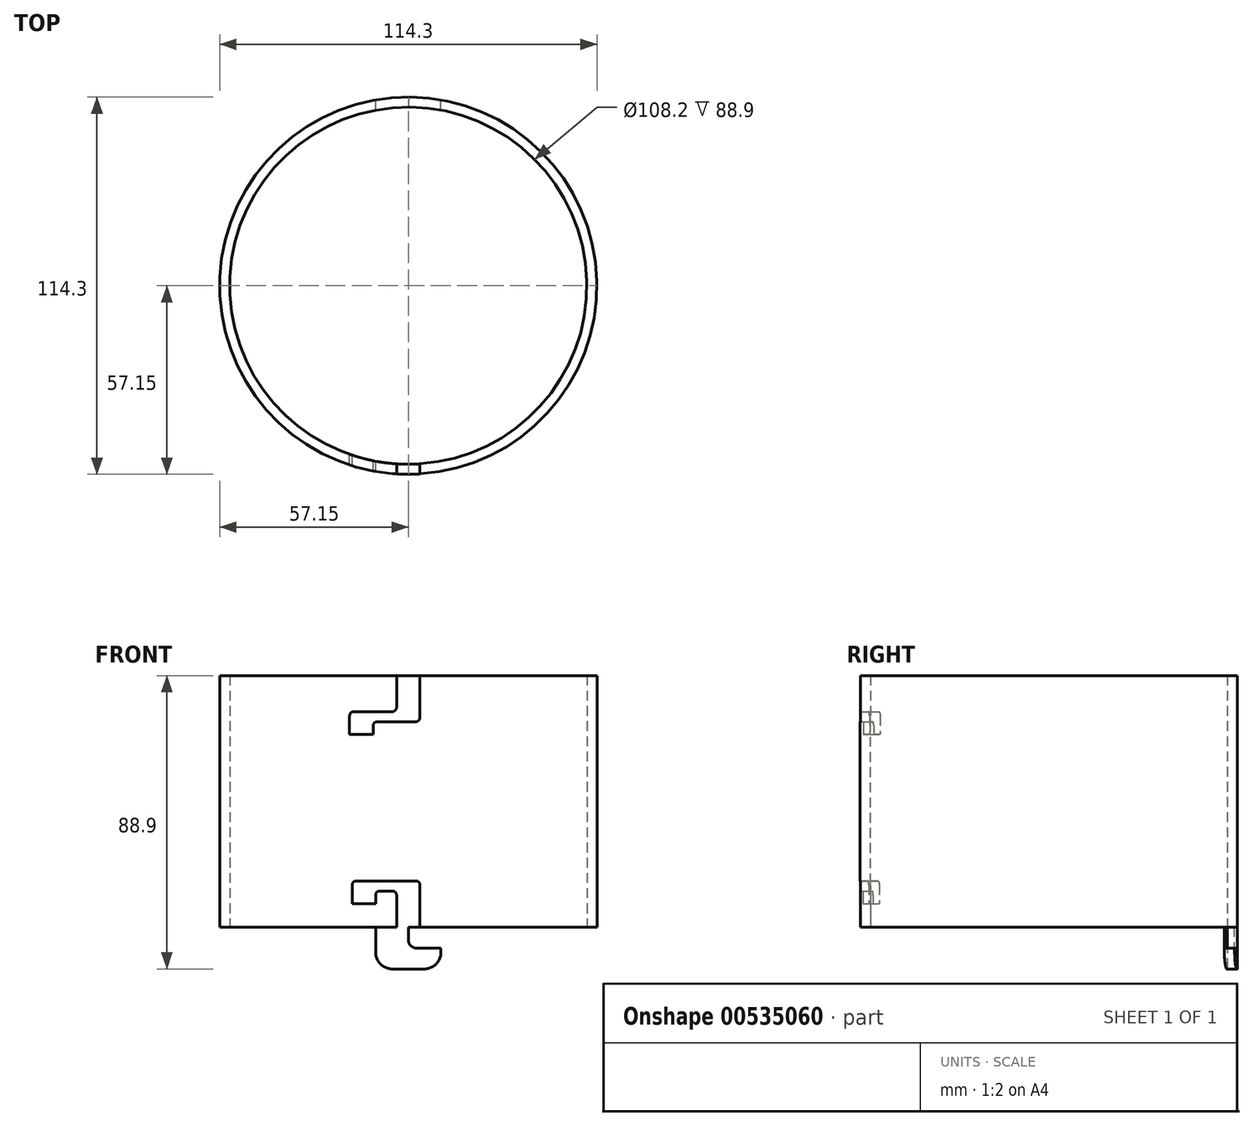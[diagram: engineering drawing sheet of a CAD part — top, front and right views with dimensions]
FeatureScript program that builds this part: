
annotation { "Feature Type Name" : "Feature", "Feature Type Description" : "" }
export const myFeature = defineFeature(function(context is Context, id is Id, definition is map)
    precondition{}
    {
        {
            var Q0;
            Q0=qCreatedBy(makeId("Top.planeOp"),FACE);
            var sketch = newSketch(context, id + "F0", { "sketchPlane" : qUnion([Q0])});
            skCircle(sketch, "E0", {"center": v(0, 0) * mm, "radius": 54.1 * mm});
            skCircle(sketch, "E1", {"center": v(0, 0) * mm, "radius": 57.15 * mm});
            skSolve(sketch);
        }
        {
            var Q0;
            Q0 = qSketchRegion(id + "F0", true);
            extrude(context, id + "F1", {"entities" : qUnion([Q0]), "depth" : 76.2 * mm, "offsetDistance" : 25.4 * mm, "symmetric" : true});
        }
        {
            var Q0;
            Q0=qCreatedBy(makeId("Front.planeOp"),FACE);
            var sketch = newSketch(context, id + "F2", { "sketchPlane" : qUnion([Q0])});
            skLineSegment(sketch, "E2", {"start": v(-3.56, -38.1) * mm, "end": v(-3.56, -27.18) * mm});
            skLineSegment(sketch, "E3", {"start": v(-3.56, -27.18) * mm, "end": v(-9.9, -27.18) * mm});
            skLineSegment(sketch, "E4", {"start": v(-9.9, -27.18) * mm, "end": v(-9.9, -30.99) * mm});
            skLineSegment(sketch, "E5", {"start": v(-9.9, -30.99) * mm, "end": v(-17.02, -30.99) * mm});
            skLineSegment(sketch, "E6", {"start": v(-17.02, -30.99) * mm, "end": v(-17.02, -24.13) * mm});
            skLineSegment(sketch, "E7", {"start": v(-17.02, -24.13) * mm, "end": v(3.56, -24.13) * mm});
            skLineSegment(sketch, "E8", {"start": v(3.56, -24.13) * mm, "end": v(3.56, -38.1) * mm});
            skPoint(sketch, "E9", {"position": v(0, -38.1) * mm});
            skPoint(sketch, "E10", {"position": v(3.56, -38.1) * mm});
            skPoint(sketch, "E11", {"position": v(-3.56, -38.1) * mm});
            skLineSegment(sketch, "E12", {"start": v(-3.56, -38.1) * mm, "end": v(3.56, -38.1) * mm});
            skPoint(sketch, "E13.MirrorP", {"position": v(-3.56, 38.1) * mm});
            skLineSegment(sketch, "E14.MirrorCS", {"start": v(-3.56, 38.1) * mm, "end": v(3.56, 38.1) * mm});
            skLineSegment(sketch, "E15.MirrorCS", {"start": v(3.56, 24.13) * mm, "end": v(3.56, 38.1) * mm});
            skLineSegment(sketch, "E16.MirrorCS", {"start": v(-3.56, 38.1) * mm, "end": v(-3.56, 27.18) * mm});
            skLineSegment(sketch, "E17", {"start": v(-3.56, 27.18) * mm, "end": v(-17.78, 27.18) * mm});
            skLineSegment(sketch, "E18", {"start": v(-17.78, 27.18) * mm, "end": v(-17.78, 20.32) * mm});
            skLineSegment(sketch, "E19", {"start": v(-17.78, 20.32) * mm, "end": v(-10.67, 20.32) * mm});
            skLineSegment(sketch, "E20", {"start": v(-10.67, 20.32) * mm, "end": v(-10.67, 24.13) * mm});
            skLineSegment(sketch, "E21", {"start": v(-10.67, 24.13) * mm, "end": v(3.56, 24.13) * mm});
            skSolve(sketch);
        }
        {
            var Q0;
            Q0 = qSketchRegion(id + "F2", true);
            extrude(context, id + "F3", {"entities" : qUnion([Q0]), "operationType" : NewBodyOperationType.REMOVE, "depth" : 103.12 * mm, "offsetDistance" : 25.4 * mm});
        }
        {
            var Q0;
            Q0=makeQuery(id+"F3.boolean.opBoolean","COPY",EDGE,{"derivedFrom":makeQuery(id+"F3.opExtrude","SWEPT_EDGE",EDGE,{"disambiguationData":[OSD([sQuery(id+"F2.wireOp",EDGE,"E3"),sQuery(id+"F2.wireOp",EDGE,"E4")])]})});
            var Q1;
            Q1=makeQuery(id+"F3.boolean.opBoolean","COPY",EDGE,{"derivedFrom":makeQuery(id+"F3.opExtrude","SWEPT_EDGE",EDGE,{"disambiguationData":[OSD([sQuery(id+"F2.wireOp",EDGE,"E2"),sQuery(id+"F2.wireOp",EDGE,"E3")])]})});
            var Q2;
            Q2=makeQuery(id+"F3.boolean.opBoolean","COPY",EDGE,{"derivedFrom":makeQuery(id+"F3.opExtrude","SWEPT_EDGE",EDGE,{"disambiguationData":[OSD([sQuery(id+"F2.wireOp",EDGE,"E7"),sQuery(id+"F2.wireOp",EDGE,"E8")])]})});
            var Q3;
            Q3=makeQuery(id+"F3.boolean.opBoolean","COPY",EDGE,{"derivedFrom":makeQuery(id+"F3.opExtrude","SWEPT_EDGE",EDGE,{"disambiguationData":[OSD([sQuery(id+"F2.wireOp",EDGE,"E6"),sQuery(id+"F2.wireOp",EDGE,"E7")])]})});
            fillet(context, id + "F4", {"entities" : qUnion([Q0, Q1, Q2, Q3]), "radius" : 1.27 * mm, "tangentPropagation" : true, "allowEdgeOverflow" : false});
        }
        {
            var Q0;
            Q0=makeQuery(id+"F3.boolean.opBoolean","COPY",EDGE,{"derivedFrom":makeQuery(id+"F3.opExtrude","SWEPT_EDGE",EDGE,{"disambiguationData":[OSD([sQuery(id+"F2.wireOp",EDGE,"E20"),sQuery(id+"F2.wireOp",EDGE,"E21")])]})});
            var Q1;
            Q1=makeQuery(id+"F3.boolean.opBoolean","COPY",EDGE,{"derivedFrom":makeQuery(id+"F3.opExtrude","SWEPT_EDGE",EDGE,{"disambiguationData":[OSD([sQuery(id+"F2.wireOp",EDGE,"E15.MirrorCS"),sQuery(id+"F2.wireOp",EDGE,"E21")])]})});
            var Q2;
            Q2=makeQuery(id+"F3.boolean.opBoolean","COPY",EDGE,{"derivedFrom":makeQuery(id+"F3.opExtrude","SWEPT_EDGE",EDGE,{"disambiguationData":[OSD([sQuery(id+"F2.wireOp",EDGE,"E16.MirrorCS"),sQuery(id+"F2.wireOp",EDGE,"E17")])]})});
            var Q3;
            Q3=makeQuery(id+"F3.boolean.opBoolean","COPY",EDGE,{"derivedFrom":makeQuery(id+"F3.opExtrude","SWEPT_EDGE",EDGE,{"disambiguationData":[OSD([sQuery(id+"F2.wireOp",EDGE,"E17"),sQuery(id+"F2.wireOp",EDGE,"E18")])]})});
            fillet(context, id + "F5", {"entities" : qUnion([Q0, Q1, Q2, Q3]), "radius" : 1.27 * mm, "tangentPropagation" : true, "allowEdgeOverflow" : false});
        }
        {
            var Q0;
            {var subQ0=sQuery(id+"F0.wireOp",EDGE,"E0");var subQ2=sQuery(id+"F0.wireOp",EDGE,"E1");var subQ4=makeQuery(id+"FeuOR3F4EdYcHin_1.1.F3.opExtrude","SWEPT_FACE",FACE,{"disambiguationData":[OSD([sQuery(id+"F2.wireOp",EDGE,"E2")])]});var subQ5=sQuery(id+"F2.wireOp",EDGE,"E8");Q0=makeQuery(id+"FeuOR3F4EdYcHin_1.2.F3.boolean.opBoolean","SPLIT",FACE,{"disambiguationData":[TD([makeQuery(id+"FeuOR3F4EdYcHin_1.1.F3.boolean.opBoolean","COPY",FACE,{"derivedFrom":subQ4})])],"derivedFrom":makeQuery(id+"FeuOR3F4EdYcHin_1.1.F3.boolean.opBoolean","SPLIT",FACE,{"disambiguationData":[TD([makeQuery(id+"F3.boolean.opBoolean","COPY",FACE,{"derivedFrom":makeQuery(id+"F3.opExtrude","SWEPT_FACE",FACE,{"disambiguationData":[OSD([subQ5])]})})])],"derivedFrom":makeQuery(id+"F1.opExtrude","CAP_FACE",FACE,{"disambiguationData":[OSD([subQ0,subQ2])],"isStart":true})})});}
            var sketch = newSketch(context, id + "F6", { "sketchPlane" : qUnion([Q0])});
            skLineSegment(sketch, "E22", {"start": v(-9.9, -53.19) * mm, "end": v(-9.9, -56.28) * mm});
            skLineSegment(sketch, "E23", {"start": v(9.9, -53.19) * mm, "end": v(9.9, -56.28) * mm});
            skSolve(sketch);
        }
        {
            var Q0;
            Q0 = qSketchRegion(id + "F6", true);
            var Q1;
            {var subQ0=sQuery(id+"F6.wireOp",EDGE,"E22");Q1=makeQuery(id+"F6.imprint","IMPRINT",FACE,{"disambiguationData":[TD([[makeQuery(id+"F6.imprint","IMPRINT",EDGE,{"derivedFrom":subQ0}),1.0]])]});}
            extrude(context, id + "F7", {"entities" : qUnion([Q0, Q1]), "operationType" : NewBodyOperationType.ADD, "depth" : 12.7 * mm, "offsetDistance" : 25.4 * mm});
        }
        {
            var Q0;
            Q0=qCreatedBy(makeId("Front.planeOp"),FACE);
            var sketch = newSketch(context, id + "F8", { "sketchPlane" : qUnion([Q0])});
            skLineSegment(sketch, "E24", {"start": v(9.9, -38.15) * mm, "end": v(0, -38.15) * mm});
            skLineSegment(sketch, "E25", {"start": v(0, -38.15) * mm, "end": v(0, -44.5) * mm});
            skLineSegment(sketch, "E26", {"start": v(0, -44.5) * mm, "end": v(9.9, -44.5) * mm});
            skLineSegment(sketch, "E27", {"start": v(9.9, -38.15) * mm, "end": v(9.9, -44.5) * mm});
            skSolve(sketch);
        }
        {
            var Q0;
            Q0 = qSketchRegion(id + "F8", true);
            extrude(context, id + "F9", {"entities" : qUnion([Q0]), "operationType" : NewBodyOperationType.REMOVE, "oppositeDirection" : true, "depth" : 73.9 * mm, "offsetDistance" : 25.4 * mm});
        }
        {
            var Q0;
            Q0=makeQuery(id+"F9.boolean.opBoolean","COPY",EDGE,{"derivedFrom":makeQuery(id+"F9.opExtrude","SWEPT_EDGE",EDGE,{"disambiguationData":[OSD([sQuery(id+"F8.wireOp",EDGE,"E25"),sQuery(id+"F8.wireOp",EDGE,"E26")])]})});
            fillet(context, id + "F10", {"entities" : qUnion([Q0]), "radius" : 2.54 * mm, "tangentPropagation" : true, "allowEdgeOverflow" : false});
        }
        {
            var Q0;
            Q0=makeQuery(id+"F7.opExtrude","CAP_EDGE",EDGE,{"disambiguationData":[OSD([sQuery(id+"F6.wireOp",EDGE,"E23")])],"isStart":false});
            var Q1;
            Q1=makeQuery(id+"F7.opExtrude","CAP_EDGE",EDGE,{"disambiguationData":[OSD([sQuery(id+"F6.wireOp",EDGE,"E22")])],"isStart":false});
            fillet(context, id + "F11", {"entities" : qUnion([Q0, Q1]), "radius" : 5.08 * mm, "tangentPropagation" : true, "allowEdgeOverflow" : false});
        }
    });
